# Revit family: НЕВАТОМ_Гибкая вставка VO, Версия 2
name_source: partatom
category: Оборудование
revit_build: Autodesk Revit 2017 (Build: 20170118_1100(x64)
units: mm (PartAtom-declared; Revit-internal decimal feet)

## family parameters
Всегда вертикально = Да
На основе рабочей плоскости = Нет
Общий = Да
При загрузке вырезать с полостями = Нет
Размер круглого соединителя = Использовать диаметр
Тип детали = Нормальный
Точка расчета площади = Нет

## types (11) — shared parameters
ADSK_Единица измерения = шт.
ADSK_Завод-изготовитель = НЕВАТОМ
ADSK_Количество = 1
ADSK_Наименование = Гибкая вставка VO
L = 240 мм
L1 = 238 мм
t = 1 мм
t1 = 241 мм
Материал = Сталь ASTM A441

## per-type parameters (varying)
| type | ADSK_Марка | ADSK_Масса | D | D1 | D2 | D_otv | b | n |
| Гибкая вставка VO №4.0 | Гибкая вставка  VO №4.0 | 2.432 | 400 мм | 430 мм | 450 мм | 398 мм | 10 мм | 10 мм |
| Гибкая вставка VO №4.5 | Гибкая вставка  VO №4.5 | 3.744 | 450 мм | 480 мм | 500 мм | 448 мм | 10 мм | 10 мм |
| Гибкая вставка VO №5.0 | Гибкая вставка  VO №5.0 | 3.2 | 500 мм | 530 мм | 550 мм | 498 мм | 11 мм | 12 мм |
| Гибкая вставка VO №5.6 | Гибкая вставка  VO №5.6 | 3.5 | 560 мм | 590 мм | 610 мм | 558 мм | 11 мм | 12 мм |
| Гибкая вставка VO №6.3 | Гибкая вставка  VO №6.3 | 4.1 | 630 мм | 660 мм | 680 мм | 628 мм | 11 мм | 12 мм |
| Гибкая вставка VO №7.1 | Гибкая вставка  VO №7.1 | 2.5 | 710 мм | 740 мм | 790 мм | 708 мм | 11 мм | 16 мм |
| Гибкая вставка VO №8.0 | Гибкая вставка  VO №8.0 | 6.3 | 800 мм | 830 мм | 864 мм | 798 мм | 11 мм | 16 мм |
| Гибкая вставка VO №9.0 | Гибкая вставка  VO №9.0 | 7.061 | 900 мм | 940 мм | 964 мм | 898 мм | 11 мм | 18 мм |
| Гибкая вставка VO №10.0 | Гибкая вставка  VO №10.0 | 10 | 1000 мм | 1040 мм | 1080 мм | 998 мм | 11 мм | 18 мм |
| Гибкая вставка VO №11.2 | Гибкая вставка  VO №11.2 | 8.752 | 1120 мм | 1160 мм | 1184 мм | 1118 мм | 11 мм | 24 мм |
| Гибкая вставка VO №12.5 | Гибкая вставка  VO №12.5 | 9.767 | 1250 мм | 1290 мм | 1330 мм | 1248 мм | 11 мм | 24 мм |
